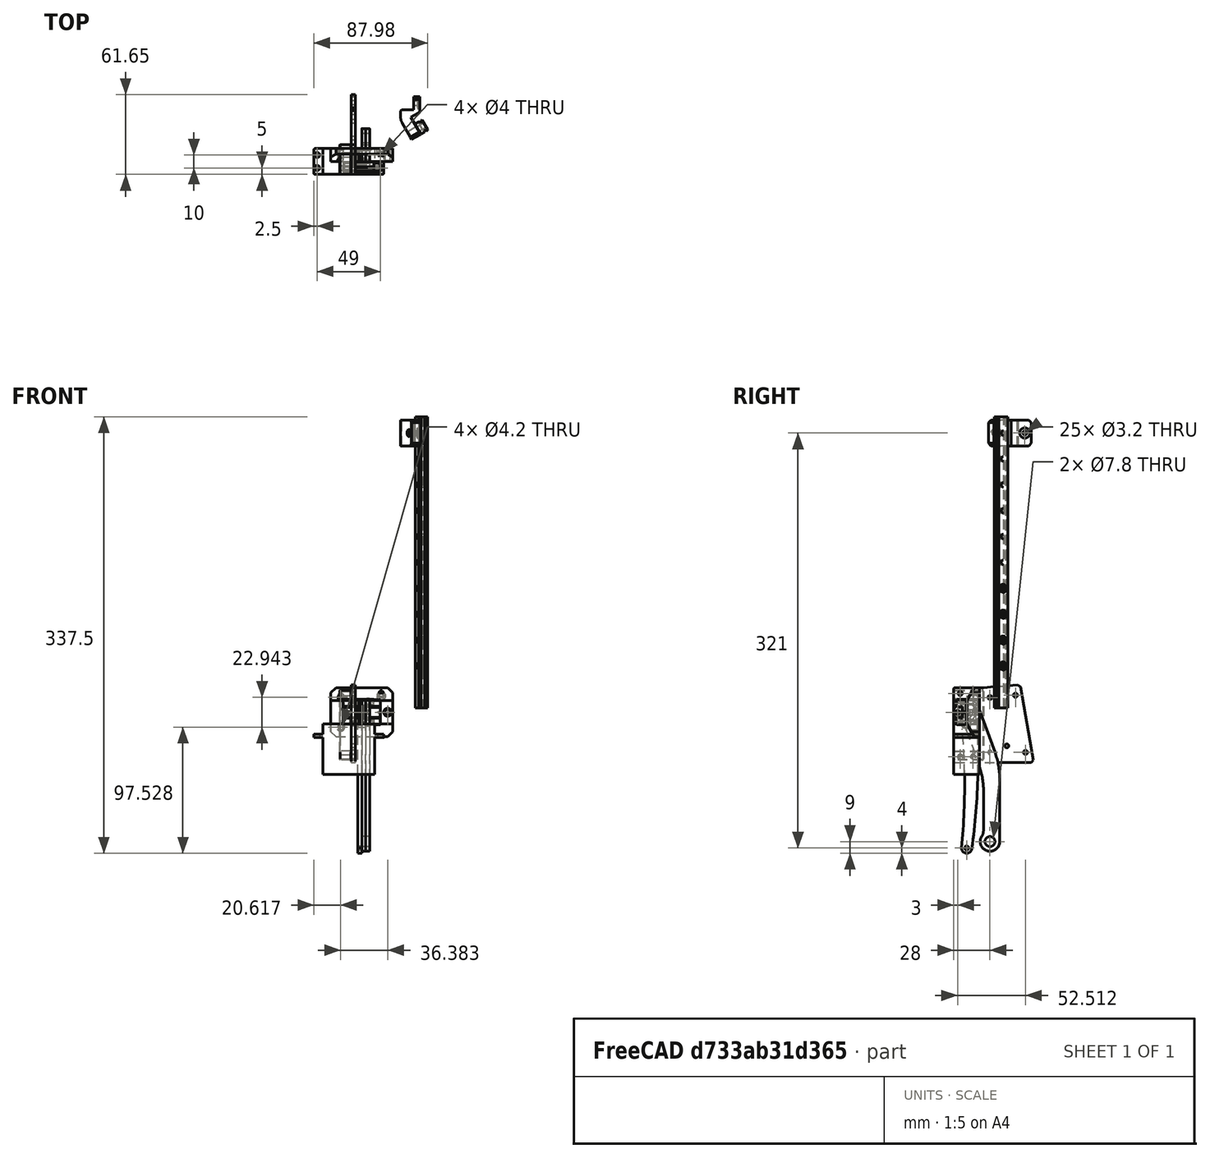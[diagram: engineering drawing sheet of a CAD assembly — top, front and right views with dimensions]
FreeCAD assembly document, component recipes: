
FREECAD ASSEMBLY — COMPONENT RECIPES ("linear-lifter")

This assembly document has 15 components, labeled P0..P14 below (a component is one placed body or linked part). 0 of them carry a construction recipe — the FreeCAD feature program that regenerates the part from scratch, quoted from this document or its linked companion documents; the rest are supplied as boundary geometry only. No exploded tour is included for this assembly.
COMPONENT P0 — geometry summary ("Bielle002"; no construction recipe available for this part):
  bounding box: 112.0 x 48.9 x 30.0 mm
  tessellated surface: 3,208 triangles
  volume: 4868 mm^3 (3% of its bounding box)
COMPONENT P1 — geometry summary ("Bielle003"; no construction recipe available for this part):
  bounding box: 112.0 x 48.9 x 30.0 mm
  tessellated surface: 3,208 triangles
  volume: 4868 mm^3 (3% of its bounding box)
COMPONENT P2 — geometry summary ("Body029"; no construction recipe available for this part):
  bounding box: 114.7 x 28.1 x 18.0 mm
  tessellated surface: 1,388 triangles
  volume: 3529 mm^3 (6% of its bounding box)
COMPONENT P3 — geometry summary ("Chariot001"; no construction recipe available for this part):
  bounding box: 48.0 x 38.0 x 10.0 mm
  tessellated surface: 8,432 triangles
  volume: 14373 mm^3 (79% of its bounding box)
COMPONENT P4 — geometry summary ("ClipRail001"; no construction recipe available for this part):
  bounding box: 27.8 x 22.0 x 20.0 mm
  tessellated surface: 2,580 triangles
  volume: 4898 mm^3 (40% of its bounding box)
  symmetry: mirror-symmetric across its z mid-plane
COMPONENT P5 — geometry summary ("ClipRail002"; no construction recipe available for this part):
  bounding box: 27.8 x 22.0 x 20.0 mm
  tessellated surface: 2,580 triangles
  volume: 4898 mm^3 (40% of its bounding box)
  symmetry: mirror-symmetric across its z mid-plane
COMPONENT P6 — geometry summary ("ClipRail003"; no construction recipe available for this part):
  bounding box: 27.8 x 22.0 x 20.0 mm
  tessellated surface: 2,580 triangles
  volume: 4898 mm^3 (40% of its bounding box)
  symmetry: mirror-symmetric across its z mid-plane
COMPONENT P7 — geometry summary ("MF001"; no construction recipe available for this part):
  bounding box: 9.2 x 8.9 x 6.9 mm
  tessellated surface: 3,376 triangles
  volume: 135 mm^3 (24% of its bounding box)
COMPONENT P8 — geometry summary ("MF002"; no construction recipe available for this part):
  bounding box: 9.2 x 8.9 x 6.9 mm
  tessellated surface: 3,376 triangles
  volume: 135 mm^3 (24% of its bounding box)
COMPONENT P9 — geometry summary ("MG997"; no construction recipe available for this part):
  bounding box: 54.0 x 46.1 x 36.8 mm
  tessellated surface: 7,492 triangles
  volume: 32310 mm^3 (35% of its bounding box)
COMPONENT P10 — geometry summary ("MGN9-225mm-Custom001"; no construction recipe available for this part):
  bounding box: 225.0 x 9.0 x 6.5 mm
  tessellated surface: 9,576 triangles
  volume: 11534 mm^3 (88% of its bounding box)
  symmetry: mirror-symmetric across its x mid-plane
COMPONENT P11 — geometry summary ("RoundServoHorn001"; no construction recipe available for this part):
  bounding box: 20.0 x 18.3 x 12.0 mm
  tessellated surface: 3,328 triangles
  volume: 697 mm^3 (16% of its bounding box)
COMPONENT P12 — geometry summary ("ServoLifterPlate001"; no construction recipe available for this part):
  bounding box: 60.3 x 54.9 x 33.4 mm
  tessellated surface: 4,100 triangles
  volume: 9315 mm^3 (8% of its bounding box)
COMPONENT P13 — geometry summary ("ServoLifterSpacer001"; no construction recipe available for this part):
  bounding box: 54.0 x 24.0 x 18.9 mm
  tessellated surface: 7,100 triangles
  volume: 3639 mm^3 (15% of its bounding box)
COMPONENT P14 — geometry summary ("mgn9c001"; no construction recipe available for this part):
  bounding box: 28.9 x 20.0 x 8.0 mm
  tessellated surface: 4,244 triangles
  volume: 3261 mm^3 (71% of its bounding box)
  symmetry: mirror-symmetric across its x mid-plane
PROVENANCE & LICENSES
A FreeCAD (.FCStd) document from a public repository crawl; recipes are the document's own serialized feature recipes (and, for linked parts, companion documents' recipes).
License: as declared in the source repository (recorded in the dataset sidecar).
